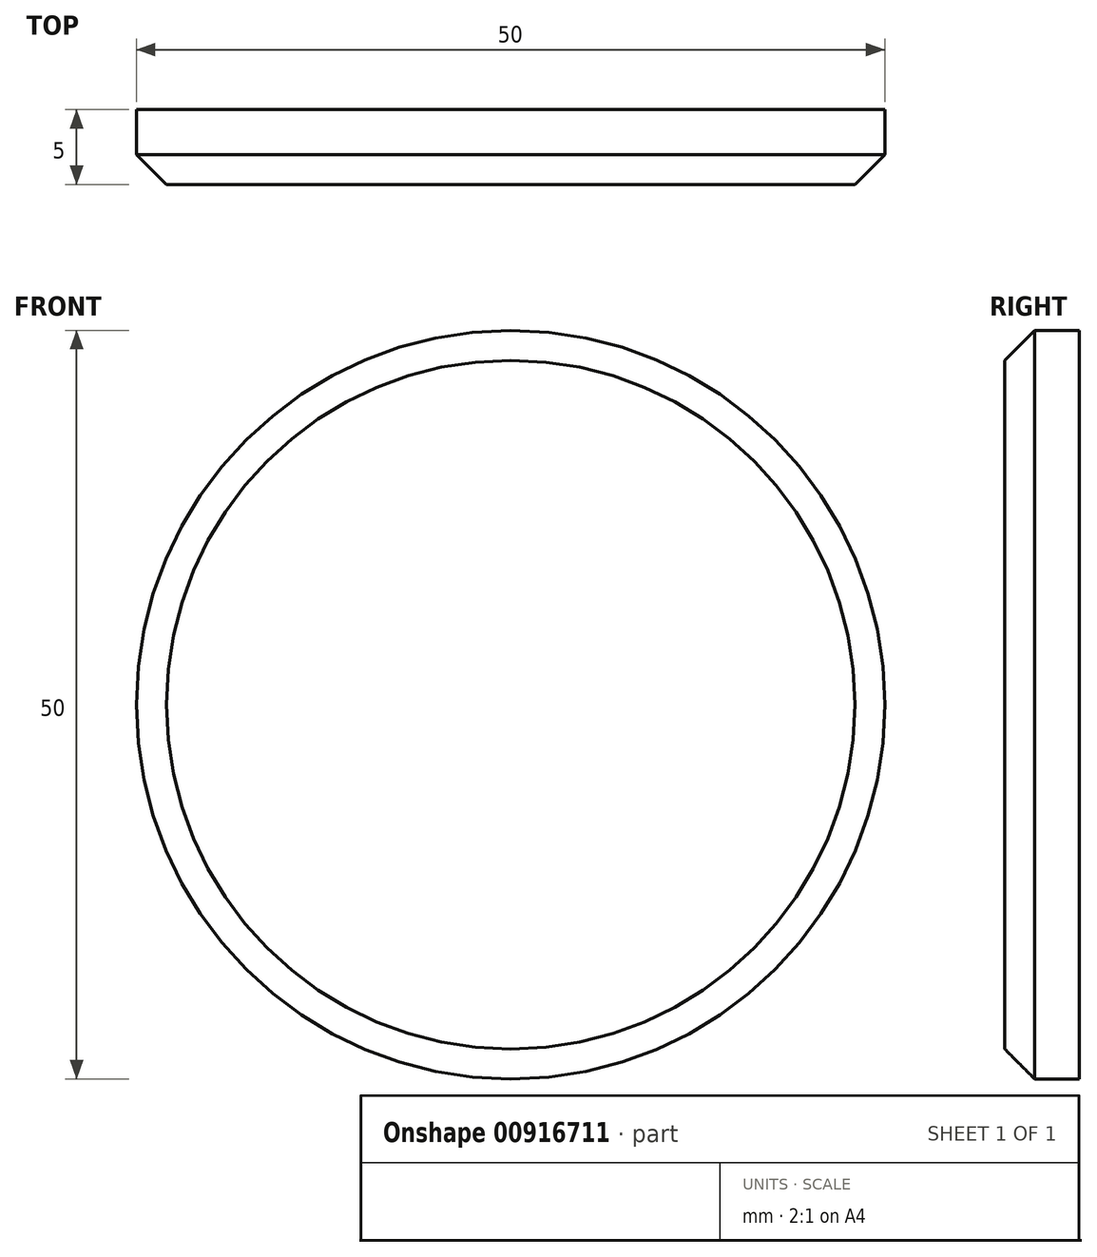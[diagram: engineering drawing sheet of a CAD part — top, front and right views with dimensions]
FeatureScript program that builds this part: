
annotation { "Feature Type Name" : "Feature", "Feature Type Description" : "" }
export const myFeature = defineFeature(function(context is Context, id is Id, definition is map)
    precondition{}
    {
        {
            var Q0;
            Q0=qCreatedBy(makeId("Front.planeOp"),FACE);
            var sketch = newSketch(context, id + "F0", { "sketchPlane" : qUnion([Q0])});
            skCircle(sketch, "E0", {"center": v(0, 0) * mm, "radius": 25 * mm});
            skSolve(sketch);
        }
        {
            var Q0;
            Q0=qCreatedBy(makeId("Right.planeOp"),FACE);
            var sketch = newSketch(context, id + "F1", { "sketchPlane" : qUnion([Q0])});
            skLineSegment(sketch, "E1", {"start": v(0, 0) * mm, "end": v(-5, 0) * mm});
            skSolve(sketch);
        }
        {
            var Q0;
            Q0=makeQuery(id+"F0.imprint","IMPRINT",FACE,{"disambiguationData":[TD([[makeQuery(id+"F0.imprint","IMPRINT",EDGE,{"derivedFrom":sQuery(id+"F0.wireOp",EDGE,"E0")}),1.0]])]});
            var Q1;
            Q1=sQuery(id+"F0.wireOp",EDGE,"E0");
            var Q2;
            Q2=sQuery(id+"F1.wireOp",EDGE,"E1");
            sweep(context, id + "F2", {"profiles" : qUnion([Q0]), "surfaceProfiles" : qUnion([Q1]), "path" : qUnion([Q2])});
        }
        {
            var Q0;
            Q0=makeQuery(id+"F2.opSweep","CAP_EDGE",EDGE,{"disambiguationData":[OSD([sQuery(id+"F0.wireOp",EDGE,"E0"),sQuery(id+"F1.wireOp",VERTEX,"E1.end")])],"isStart":false});
            chamfer(context, id + "F3", {"entities" : qUnion([Q0]), "width" : 2 * mm, "tangentPropagation" : true});
        }
    });
